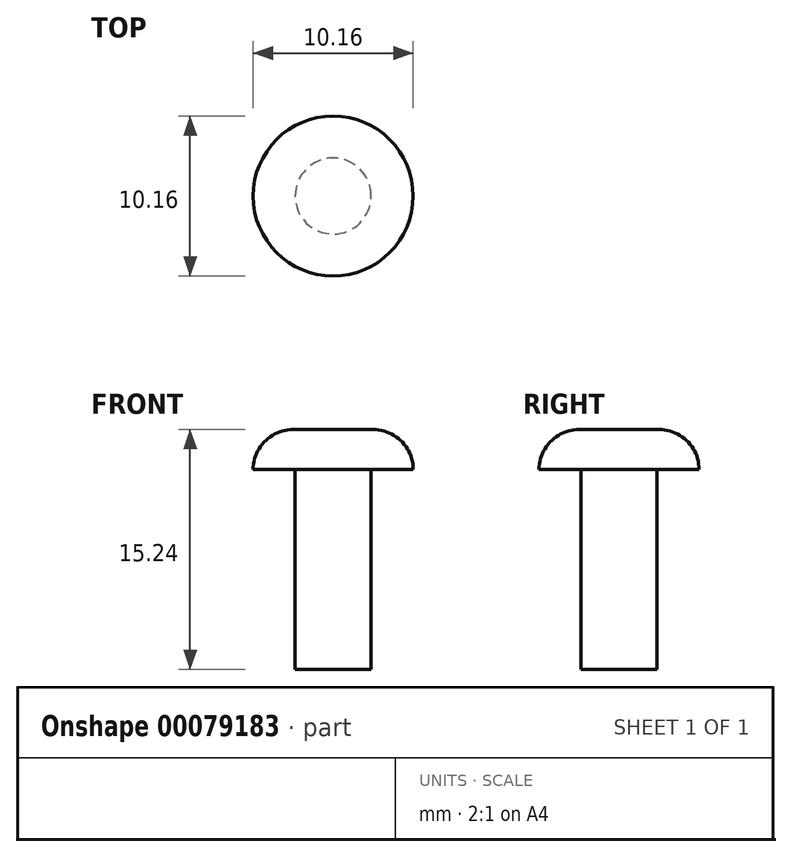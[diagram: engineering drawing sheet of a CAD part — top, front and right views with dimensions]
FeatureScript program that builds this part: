
annotation { "Feature Type Name" : "Feature", "Feature Type Description" : "" }
export const myFeature = defineFeature(function(context is Context, id is Id, definition is map)
    precondition{}
    {
        {
            var Q0;
            Q0=qCreatedBy(makeId("Top.planeOp"),FACE);
            var sketch = newSketch(context, id + "F0", { "sketchPlane" : qUnion([Q0])});
            skCircle(sketch, "E0", {"center": v(0, 0) * mm, "radius": 2.41 * mm});
            skSolve(sketch);
        }
        {
            var Q0;
            Q0=qSketchRegion(id+"F0",true);
            extrude(context, id + "F1", {"entities" : qUnion([Q0]), "depth" : 12.7 * mm});
        }
        {
            var Q0;
            Q0=makeQuery(id+"F1.opExtrude","CAP_FACE",FACE,{"disambiguationData":[OSD([sQuery(id+"F0.wireOp",EDGE,"E0")])],"isStart":false});
            var sketch = newSketch(context, id + "F2", { "sketchPlane" : qUnion([Q0])});
            skCircle(sketch, "E1", {"center": v(0, 0) * mm, "radius": 5.08 * mm});
            skSolve(sketch);
        }
        {
            var Q0;
            Q0=qSketchRegion(id+"F2",true);
            extrude(context, id + "F3", {"entities" : qUnion([Q0]), "operationType" : NewBodyOperationType.ADD, "depth" : 2.54 * mm});
        }
        {
            var Q0;
            Q0=makeQuery(id+"F3.opExtrude","CAP_EDGE",EDGE,{"disambiguationData":[OSD([sQuery(id+"F2.wireOp",EDGE,"E1")])],"isStart":false});
            fillet(context, id + "F4", {"entities" : qUnion([Q0]), "radius" : 2.54 * mm, "tangentPropagation" : true, "allowEdgeOverflow" : false});
        }
    });
